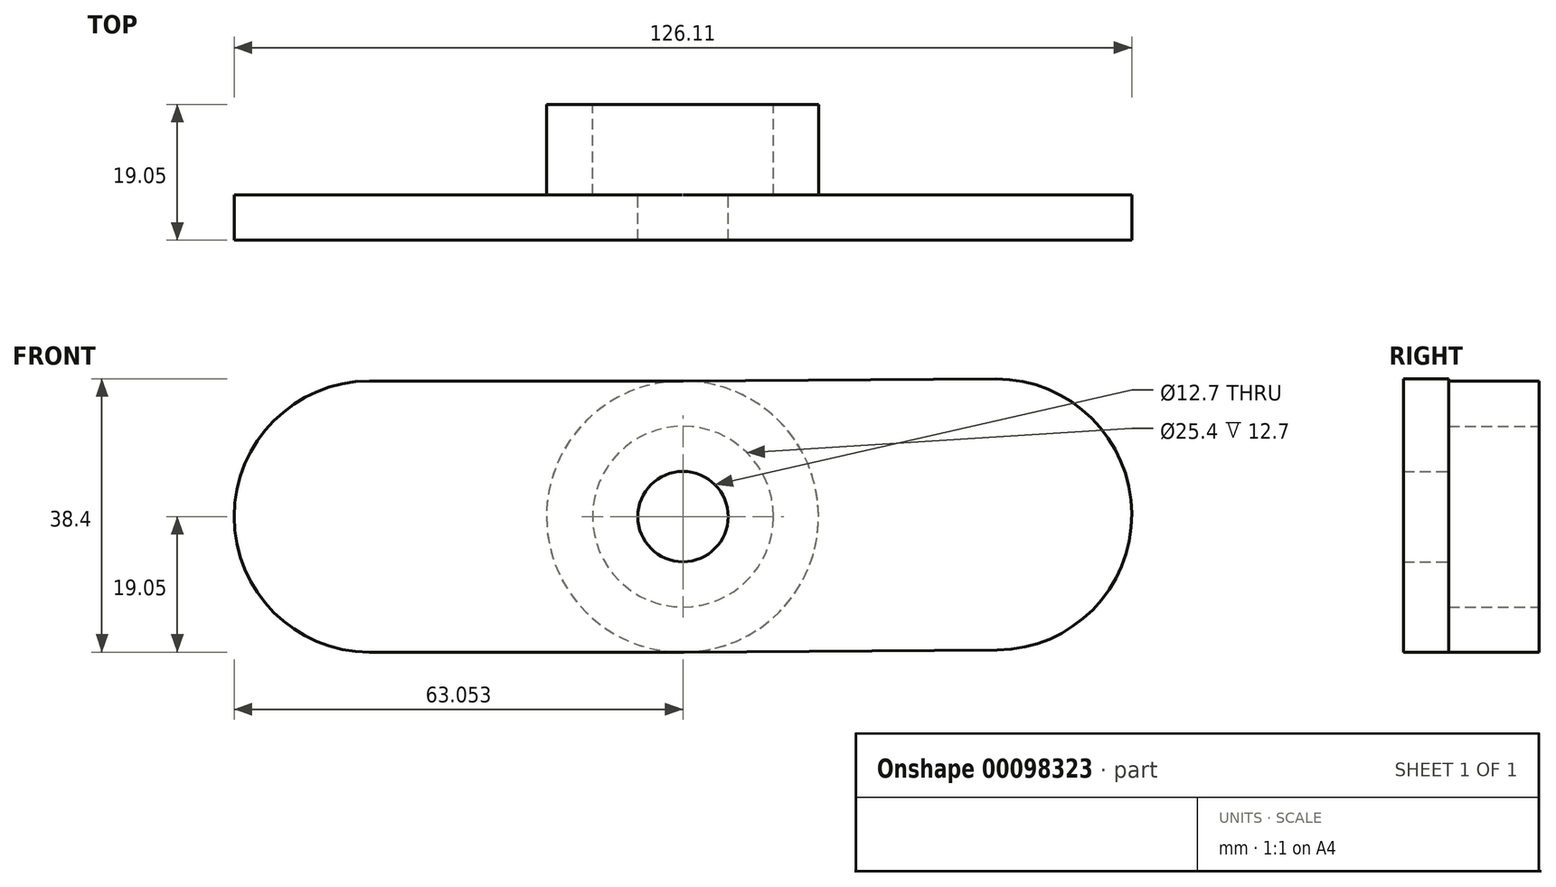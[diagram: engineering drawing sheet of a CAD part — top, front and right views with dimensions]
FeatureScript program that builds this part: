
annotation { "Feature Type Name" : "Feature", "Feature Type Description" : "" }
export const myFeature = defineFeature(function(context is Context, id is Id, definition is map)
    precondition{}
    {
        {
            var Q0;
            Q0=qCreatedBy(makeId("Front.planeOp"),FACE);
            var sketch = newSketch(context, id + "F0", { "sketchPlane" : qUnion([Q0])});
            skCircle(sketch, "E0", {"center": v(61.57, 0) * mm, "radius": 12.7 * mm});
            skCircle(sketch, "E1", {"center": v(61.57, 0) * mm, "radius": 6.35 * mm});
            skLineSegment(sketch, "E2.0", {"start": v(17.52, -19.05) * mm, "end": v(61.57, -19.05) * mm});
            skArc(sketch, "E2.1", {"start": v(17.52, 19.05) * mm, "mid": v(-1.48, 0) * mm, "end": v(17.52, -19.05) * mm});
            skLineSegment(sketch, "E2.2", {"start": v(17.52, 19.05) * mm, "end": v(61.46, 19.05) * mm});
            skArc(sketch, "E3.trimOffspring", {"start": v(61.57, -19.05) * mm, "mid": v(80.62, 0.06) * mm, "end": v(61.46, 19.05) * mm});
            skArc(sketch, "E4", {"start": v(61.46, 19.05) * mm, "mid": v(42.4, -0.06) * mm, "end": v(61.57, -19.05) * mm});
            skLineSegment(sketch, "E5", {"start": v(61.57, 0) * mm, "end": v(61.57, -32.9) * mm});
            skLineSegment(sketch, "E6.MirrorCS", {"start": v(105.76, -18.75) * mm, "end": v(61.7, -19.05) * mm});
            skArc(sketch, "E7.MirrorCS", {"start": v(105.5, 19.35) * mm, "mid": v(124.63, 0.42) * mm, "end": v(105.76, -18.75) * mm});
            skLineSegment(sketch, "E8.MirrorCS", {"start": v(105.5, 19.35) * mm, "end": v(61.56, 19.05) * mm});
            skSolve(sketch);
        }
        {
            var Q0;
            Q0 = qSketchRegion(id + "F0", true);
            var Q1;
            Q1=makeQuery(id+"F0.imprint","IMPRINT",FACE,{"disambiguationData":[TD([[makeQuery(id+"F0.imprint","IMPRINT",EDGE,{"derivedFrom":sQuery(id+"F0.wireOp",EDGE,"E0")}),1.0]])]});
            extrude(context, id + "F1", {"entities" : qUnion([Q0, Q1]), "depth" : 19.05 * mm});
        }
        {
            var Q0;
            Q0=makeQuery(id+"F0.imprint","IMPRINT",FACE,{"disambiguationData":[TD([[makeQuery(id+"F0.imprint","IMPRINT",EDGE,{"derivedFrom":sQuery(id+"F0.wireOp",EDGE,"E0")}),1.0]])]});
            var Q1;
            {var subQ0=sQuery(id+"F0.wireOp",EDGE,"E2.1");Q1=makeQuery(id+"F0.imprint","IMPRINT",FACE,{"disambiguationData":[TD([[makeQuery(id+"F0.imprint","IMPRINT",EDGE,{"derivedFrom":subQ0}),1.0]])]});}
            extrude(context, id + "F2", {"entities" : qUnion([Q0, Q1]), "operationType" : NewBodyOperationType.REMOVE, "depth" : 12.7 * mm});
        }
        {
            var Q0;
            {var subQ0=sQuery(id+"F0.wireOp",EDGE,"E6.MirrorCS");Q0=makeQuery(id+"F0.imprint","IMPRINT",FACE,{"disambiguationData":[TD([[makeQuery(id+"F0.imprint","IMPRINT",EDGE,{"derivedFrom":subQ0}),-1.0]])]});}
            extrude(context, id + "F3", {"entities" : qUnion([Q0]), "operationType" : NewBodyOperationType.REMOVE, "depth" : 12.7 * mm});
        }
    });
